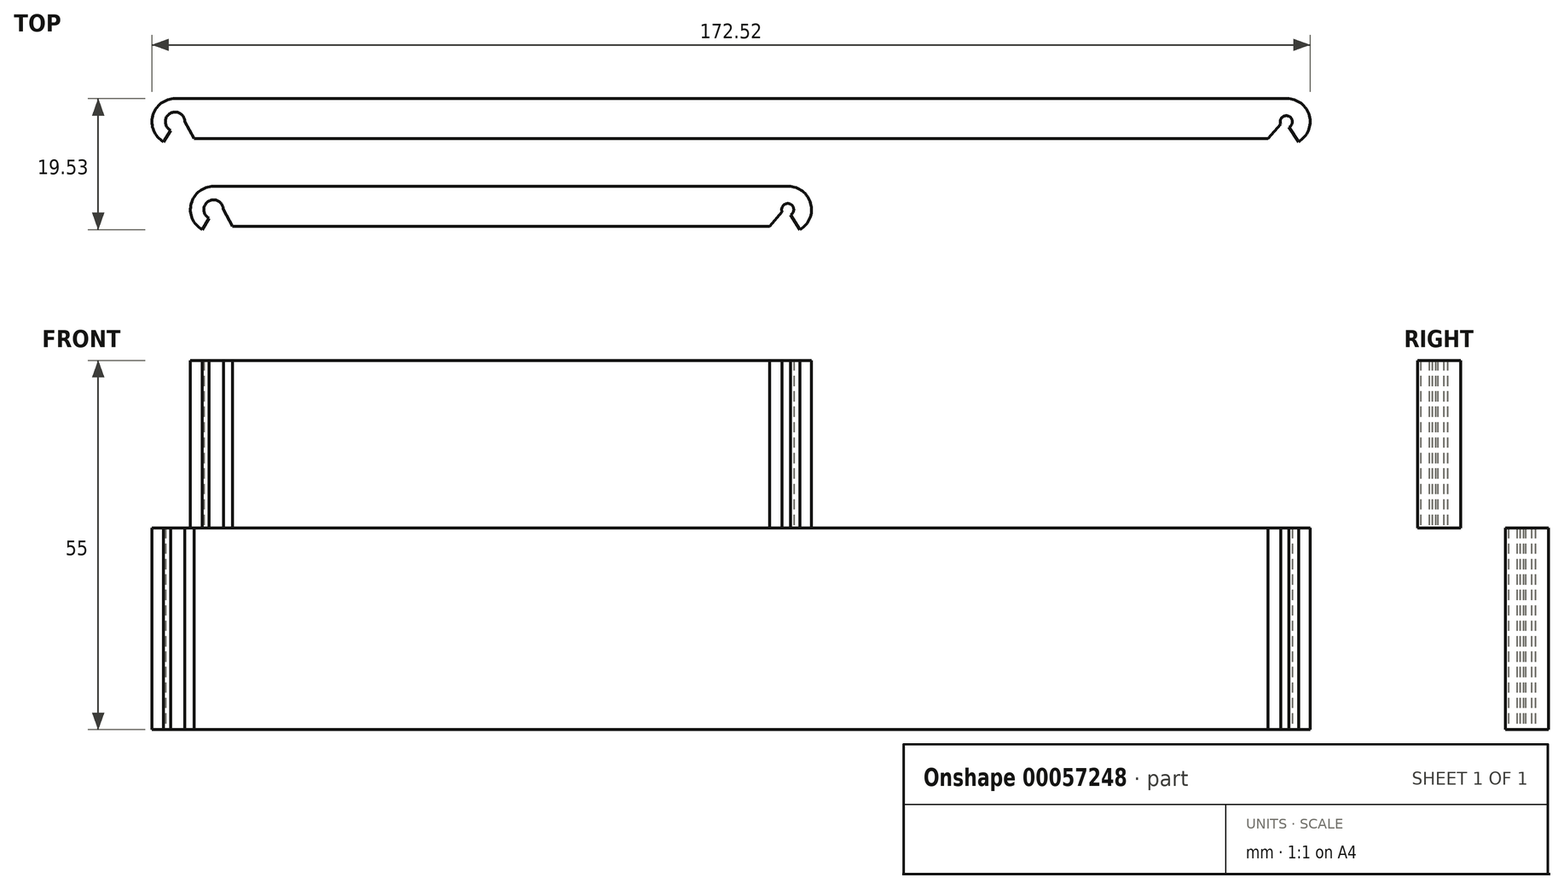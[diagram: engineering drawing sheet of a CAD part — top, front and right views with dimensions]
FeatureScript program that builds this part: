
annotation { "Feature Type Name" : "Feature", "Feature Type Description" : "" }
export const myFeature = defineFeature(function(context is Context, id is Id, definition is map)
    precondition{}
    {
        {
            var Q0;
            Q0=qCreatedBy(makeId("Top.planeOp"),FACE);
            var sketch = newSketch(context, id + "F0", { "sketchPlane" : qUnion([Q0])});
            skLineSegment(sketch, "E0", {"start": v(-40, 0) * mm, "end": v(124.62, 0) * mm, "construction": true});
            skArc(sketch, "E1", {"start": v(-38.55, 0) * mm, "mid": v(-40.75, 1.24) * mm, "end": v(-40.67, -1.28) * mm});
            skArc(sketch, "E2.0", {"start": v(-40, 3.45) * mm, "mid": v(-43.33, 0.9) * mm, "end": v(-41.72, -3) * mm});
            skLineSegment(sketch, "E3", {"start": v(-40, 3.45) * mm, "end": v(42.8, 3.45) * mm});
            skLineSegment(sketch, "E4", {"start": v(-34.7, 0) * mm, "end": v(-38.55, 0) * mm});
            skLineSegment(sketch, "E5", {"start": v(-37.2, -2.52) * mm, "end": v(-38.55, 0) * mm});
            skLineSegment(sketch, "E6", {"start": v(-37.2, -2.52) * mm, "end": v(42.8, -2.52) * mm});
            skLineSegment(sketch, "E7", {"start": v(-40.67, -1.28) * mm, "end": v(-41.72, -3) * mm});
            skLineSegment(sketch, "E8", {"start": v(42.8, -2.52) * mm, "end": v(42.8, 3.45) * mm});
            skLineSegment(sketch, "E9.MirrorCS", {"start": v(125.91, -0.8) * mm, "end": v(127.34, -3) * mm});
            skArc(sketch, "E10.MirrorCS", {"start": v(125.62, 3.45) * mm, "mid": v(128.95, 0.9) * mm, "end": v(127.34, -3) * mm});
            skLineSegment(sketch, "E11.MirrorCS", {"start": v(125.62, 3.45) * mm, "end": v(42.8, 3.45) * mm});
            skLineSegment(sketch, "E12.MirrorCS", {"start": v(122.8, -2.52) * mm, "end": v(42.8, -2.52) * mm});
            skArc(sketch, "E13", {"start": v(125.91, -0.8) * mm, "mid": v(125.85, 0.84) * mm, "end": v(124.68, -0.32) * mm});
            skLineSegment(sketch, "E14", {"start": v(124.68, -0.32) * mm, "end": v(122.8, -2.52) * mm});
            skSolve(sketch);
        }
        {
            var Q0;
            Q0 = qSketchRegion(id + "F0", true);
            extrude(context, id + "F1", {"entities" : qUnion([Q0]), "depth" : 30 * mm});
        }
        {
            var Q0;
            Q0=makeQuery(id+"F1.opExtrude","CAP_FACE",FACE,{"disambiguationData":[OSD([sQuery(id+"F0.wireOp",EDGE,"E1"),sQuery(id+"F0.wireOp",EDGE,"E2.0"),sQuery(id+"F0.wireOp",EDGE,"E3"),sQuery(id+"F0.wireOp",EDGE,"GSWsLBvE-1WsK-Lprn-xL4K-RToTh8AcNkuf"),sQuery(id+"F0.wireOp",EDGE,"coFZlaGe-CMsh-JLGU-xktg-yzyGsjlMlQ7o"),sQuery(id+"F0.wireOp",EDGE,"E5"),sQuery(id+"F0.wireOp",EDGE,"E6"),sQuery(id+"F0.wireOp",EDGE,"E7")])],"isStart":false});
            var sketch = newSketch(context, id + "F2", { "sketchPlane" : qUnion([Q0])});
            skLineSegment(sketch, "E15", {"start": v(-34.27, -13.09) * mm, "end": v(50.35, -13.09) * mm, "construction": true});
            skLineSegment(sketch, "E16.MirrorCS", {"start": v(51.35, -9.64) * mm, "end": v(8.54, -9.64) * mm});
            skArc(sketch, "E17.MirrorCS", {"start": v(51.35, -9.64) * mm, "mid": v(54.68, -12.2) * mm, "end": v(53.07, -16.08) * mm});
            skLineSegment(sketch, "E18.MirrorCS", {"start": v(48.54, -15.6) * mm, "end": v(8.54, -15.6) * mm});
            skLineSegment(sketch, "E19", {"start": v(-34.27, -9.64) * mm, "end": v(8.54, -9.64) * mm});
            skArc(sketch, "E20.0", {"start": v(-34.27, -9.64) * mm, "mid": v(-37.6, -12.2) * mm, "end": v(-35.99, -16.08) * mm});
            skLineSegment(sketch, "E21", {"start": v(-31.46, -15.6) * mm, "end": v(8.54, -15.6) * mm});
            skLineSegment(sketch, "E22", {"start": v(-28.97, -13.09) * mm, "end": v(-32.82, -13.09) * mm});
            skLineSegment(sketch, "E23.MirrorCS", {"start": v(51.64, -13.9) * mm, "end": v(53.07, -16.08) * mm});
            skLineSegment(sketch, "E24", {"start": v(-34.94, -14.37) * mm, "end": v(-35.99, -16.08) * mm});
            skArc(sketch, "E25", {"start": v(-32.82, -13.09) * mm, "mid": v(-35.02, -11.85) * mm, "end": v(-34.94, -14.37) * mm});
            skLineSegment(sketch, "E26", {"start": v(-31.46, -15.6) * mm, "end": v(-32.82, -13.09) * mm});
            skArc(sketch, "E27", {"start": v(51.64, -13.9) * mm, "mid": v(51.58, -12.25) * mm, "end": v(50.41, -13.4) * mm});
            skLineSegment(sketch, "E28", {"start": v(50.41, -13.4) * mm, "end": v(48.54, -15.6) * mm});
            skSolve(sketch);
        }
        {
            var Q0;
            Q0=makeQuery(id+"F2.imprint","IMPRINT",FACE,{"disambiguationData":[TD([[makeQuery(id+"F2.imprint","IMPRINT",EDGE,{"derivedFrom":sQuery(id+"F2.wireOp",EDGE,"E16.MirrorCS")}),1.0]])]});
            extrude(context, id + "F3", {"entities" : qUnion([Q0]), "depth" : 25 * mm});
        }
    });
